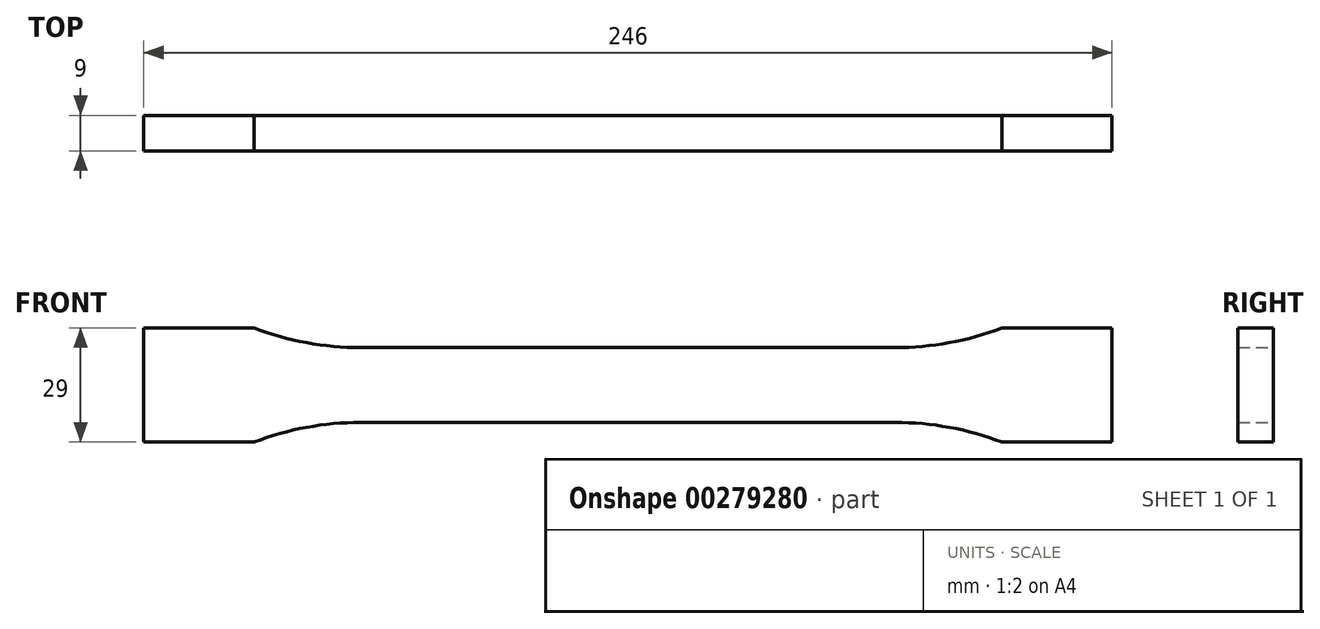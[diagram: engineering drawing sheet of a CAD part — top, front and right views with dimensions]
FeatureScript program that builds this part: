
annotation { "Feature Type Name" : "Feature", "Feature Type Description" : "" }
export const myFeature = defineFeature(function(context is Context, id is Id, definition is map)
    precondition{}
    {
        {
            var Q0;
            Q0=qCreatedBy(makeId("Front.planeOp"),FACE);
            var sketch = newSketch(context, id + "F0", { "sketchPlane" : qUnion([Q0])});
            skLineSegment(sketch, "E0", {"start": v(0, 9.5) * mm, "end": v(67.89, 9.5) * mm});
            skArc(sketch, "E1", {"start": v(67.89, 9.5) * mm, "mid": v(81.67, 10.76) * mm, "end": v(95, 14.5) * mm});
            skLineSegment(sketch, "E2", {"start": v(95, 14.5) * mm, "end": v(123, 14.5) * mm});
            skLineSegment(sketch, "E3.MirrorCS", {"start": v(95, -14.5) * mm, "end": v(123, -14.5) * mm});
            skLineSegment(sketch, "E4.MirrorCS", {"start": v(0, -9.5) * mm, "end": v(67.89, -9.5) * mm});
            skArc(sketch, "E5.MirrorCS", {"start": v(67.89, -9.5) * mm, "mid": v(81.67, -10.76) * mm, "end": v(95, -14.5) * mm});
            skLineSegment(sketch, "E6.MirrorCS", {"start": v(0, 9.5) * mm, "end": v(-67.89, 9.5) * mm});
            skArc(sketch, "E7.MirrorCS", {"start": v(-67.89, 9.5) * mm, "mid": v(-81.67, 10.76) * mm, "end": v(-95, 14.5) * mm});
            skLineSegment(sketch, "E8.MirrorCS", {"start": v(-95, 14.5) * mm, "end": v(-123, 14.5) * mm});
            skLineSegment(sketch, "E9.MirrorCS", {"start": v(-95, -14.5) * mm, "end": v(-123, -14.5) * mm});
            skArc(sketch, "E10.MirrorCS", {"start": v(-67.89, -9.5) * mm, "mid": v(-81.67, -10.76) * mm, "end": v(-95, -14.5) * mm});
            skLineSegment(sketch, "E11.MirrorCS", {"start": v(0, -9.5) * mm, "end": v(-67.89, -9.5) * mm});
            skLineSegment(sketch, "E12", {"start": v(-123, 14.5) * mm, "end": v(-123, -14.5) * mm});
            skLineSegment(sketch, "E13", {"start": v(123, 14.5) * mm, "end": v(123, -14.5) * mm});
            skSolve(sketch);
        }
        {
            var Q0;
            Q0 = qSketchRegion(id + "F0", true);
            extrude(context, id + "F1", {"entities" : qUnion([Q0]), "endBound" : BoundingType.SYMMETRIC, "depth" : 9 * mm});
        }
    });
